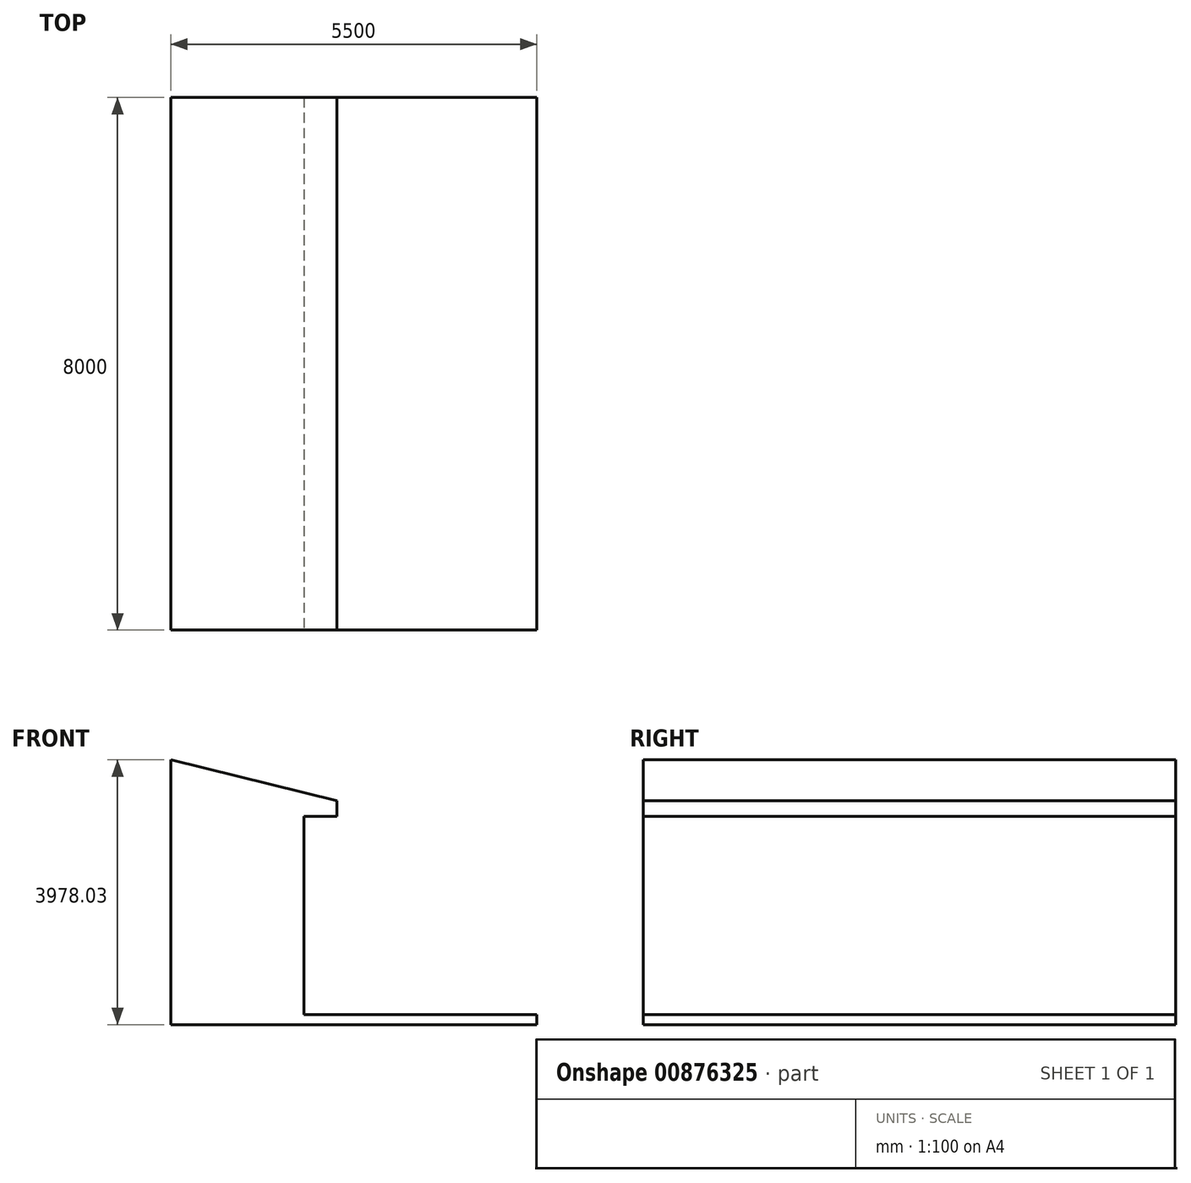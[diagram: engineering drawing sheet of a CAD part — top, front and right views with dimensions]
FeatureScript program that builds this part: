
annotation { "Feature Type Name" : "Feature", "Feature Type Description" : "" }
export const myFeature = defineFeature(function(context is Context, id is Id, definition is map)
    precondition{}
    {
        {
            var Q0;
            Q0=qCreatedBy(makeId("Front.planeOp"),FACE);
            var sketch = newSketch(context, id + "F0", { "sketchPlane" : qUnion([Q0])});
            skLineSegment(sketch, "E0", {"start": v(2000, 31.97) * mm, "end": v(2000, 3006.97) * mm});
            skLineSegment(sketch, "E1", {"start": v(2000, 3006.97) * mm, "end": v(2500, 3006.97) * mm});
            skLineSegment(sketch, "E2", {"start": v(2500, 3006.97) * mm, "end": v(2500, 3246.97) * mm});
            skLineSegment(sketch, "E3", {"start": v(2500, 3246.97) * mm, "end": v(0, 3860) * mm});
            skLineSegment(sketch, "E4", {"start": v(0, 0) * mm, "end": v(0, 3860) * mm});
            skLineSegment(sketch, "E5", {"start": v(0, 3860) * mm, "end": v(0, 3860) * mm});
            skLineSegment(sketch, "E6", {"start": v(2000, 31.97) * mm, "end": v(5500, 31.97) * mm});
            skLineSegment(sketch, "E7", {"start": v(5500, 31.97) * mm, "end": v(5500, -118.03) * mm});
            skLineSegment(sketch, "E8", {"start": v(5500, -118.03) * mm, "end": v(0, -118.03) * mm});
            skLineSegment(sketch, "E9", {"start": v(0, -118.03) * mm, "end": v(0, 0) * mm});
            skSolve(sketch);
        }
        {
            var Q0;
            Q0=qCreatedBy(makeId("Right.planeOp"),FACE);
            var sketch = newSketch(context, id + "F1", { "sketchPlane" : qUnion([Q0])});
            skLineSegment(sketch, "E10", {"start": v(0, 0) * mm, "end": v(-8000, 0) * mm});
            skSolve(sketch);
        }
        {
            var Q0;
            Q0=makeQuery(id+"F0.imprint","IMPRINT",FACE,{"disambiguationData":[TD([[makeQuery(id+"F0.imprint","IMPRINT",EDGE,{"derivedFrom":sQuery(id+"F0.wireOp",EDGE,"5p35PY19-Qcm2-I6LI-YYMA-YpI3xkug17Lr")}),1.0]])]});
            var Q1;
            Q1=makeQuery(id+"F0.imprint","IMPRINT",FACE,{"disambiguationData":[TD([[makeQuery(id+"F0.imprint","IMPRINT",EDGE,{"derivedFrom":sQuery(id+"F0.wireOp",EDGE,"E0")}),1.0]])]});
            var Q2;
            Q2=sQuery(id+"F1.wireOp",EDGE,"E10");
            sweep(context, id + "F2", {"profiles" : qUnion([Q0, Q1]), "path" : qUnion([Q2])});
        }
    });
